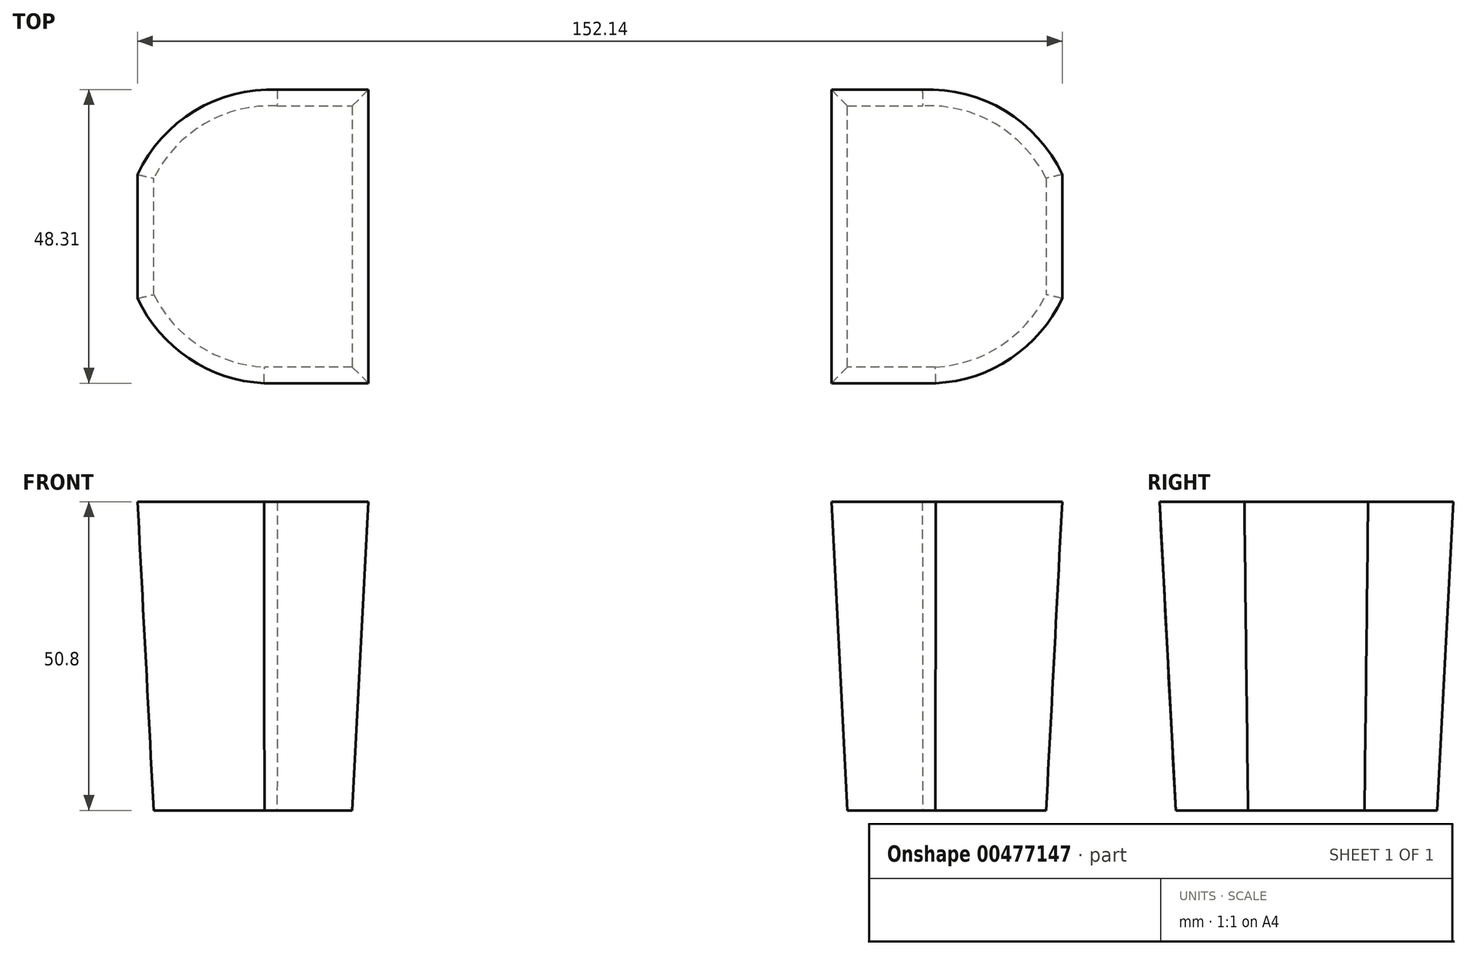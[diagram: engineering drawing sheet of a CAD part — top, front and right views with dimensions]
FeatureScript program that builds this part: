
annotation { "Feature Type Name" : "Feature", "Feature Type Description" : "" }
export const myFeature = defineFeature(function(context is Context, id is Id, definition is map)
    precondition{}
    {
        {
            var Q0;
            Q0=qCreatedBy(makeId("Top.planeOp"),FACE);
            var sketch = newSketch(context, id + "F0", { "sketchPlane" : qUnion([Q0])});
            skLineSegment(sketch, "E0.bottom", {"start": v(-53.12, 21.39) * mm, "end": v(-40.74, 21.39) * mm});
            skLineSegment(sketch, "E0.top", {"start": v(-55.2, -21.57) * mm, "end": v(-40.74, -21.57) * mm});
            skLineSegment(sketch, "E0.left", {"start": v(-73.4, 9.49) * mm, "end": v(-73.4, -9.67) * mm});
            skLineSegment(sketch, "E0.right", {"start": v(-40.74, 21.39) * mm, "end": v(-40.74, -21.57) * mm});
            skArc(sketch, "E1", {"start": v(-53.12, 21.39) * mm, "mid": v(-65.03, 18.46) * mm, "end": v(-73.4, 9.49) * mm});
            skArc(sketch, "E2.trimOffspring", {"start": v(-73.4, -9.67) * mm, "mid": v(-65.03, -18.64) * mm, "end": v(-53.12, -21.57) * mm});
            skLineSegment(sketch, "E3.MirrorCS", {"start": v(53.12, 21.39) * mm, "end": v(40.74, 21.39) * mm});
            skLineSegment(sketch, "E4.MirrorCS", {"start": v(55.2, -21.57) * mm, "end": v(40.74, -21.57) * mm});
            skLineSegment(sketch, "E5.MirrorCS", {"start": v(40.74, 21.39) * mm, "end": v(40.74, -21.57) * mm});
            skLineSegment(sketch, "E6.MirrorCS", {"start": v(73.4, 9.49) * mm, "end": v(73.4, -9.67) * mm});
            skArc(sketch, "E7.MirrorCS", {"start": v(53.12, 21.39) * mm, "mid": v(65.03, 18.46) * mm, "end": v(73.4, 9.49) * mm});
            skArc(sketch, "E8.MirrorCS", {"start": v(73.4, -9.67) * mm, "mid": v(65.03, -18.64) * mm, "end": v(53.12, -21.57) * mm});
            skLineSegment(sketch, "E9", {"start": v(-37.42, -21.57) * mm, "end": v(36.88, 21.39) * mm});
            skLineSegment(sketch, "E10", {"start": v(-37.42, 21.39) * mm, "end": v(36.88, -21.57) * mm});
            skPoint(sketch, "E10.startSnap0", {"position": v(-46.93, 21.39) * mm});
            skSolve(sketch);
        }
        {
            var Q0;
            Q0=makeQuery(id+"F0.imprint","IMPRINT",FACE,{"disambiguationData":[TD([[makeQuery(id+"F0.imprint","IMPRINT",EDGE,{"derivedFrom":sQuery(id+"F0.wireOp",EDGE,"E0.bottom")}),-1.0]])]});
            var Q1;
            Q1=makeQuery(id+"F0.imprint","IMPRINT",FACE,{"disambiguationData":[TD([[makeQuery(id+"F0.imprint","IMPRINT",EDGE,{"derivedFrom":sQuery(id+"F0.wireOp",EDGE,"E3.MirrorCS")}),1.0]])]});
            extrude(context, id + "F1", {"entities" : qUnion([Q0, Q1]), "depth" : 50.8 * mm, "hasDraft" : true, "draftAngle" : 3 * degree});
        }
        {
            var Q0;
            Q0=sQuery(id+"F0.wireOp",EDGE,"E10");
            extrude(context, id + "F2", {"bodyType" : ToolBodyType.SURFACE, "surfaceEntities" : qUnion([Q0]), "oppositeDirection" : true, "depth" : 101.6 * mm});
        }
        {
            var Q0;
            Q0=sQuery(id+"F0.wireOp",EDGE,"E9");
            extrude(context, id + "F3", {"bodyType" : ToolBodyType.SURFACE, "surfaceEntities" : qUnion([Q0]), "oppositeDirection" : true, "depth" : 50.8 * mm});
        }
    });
